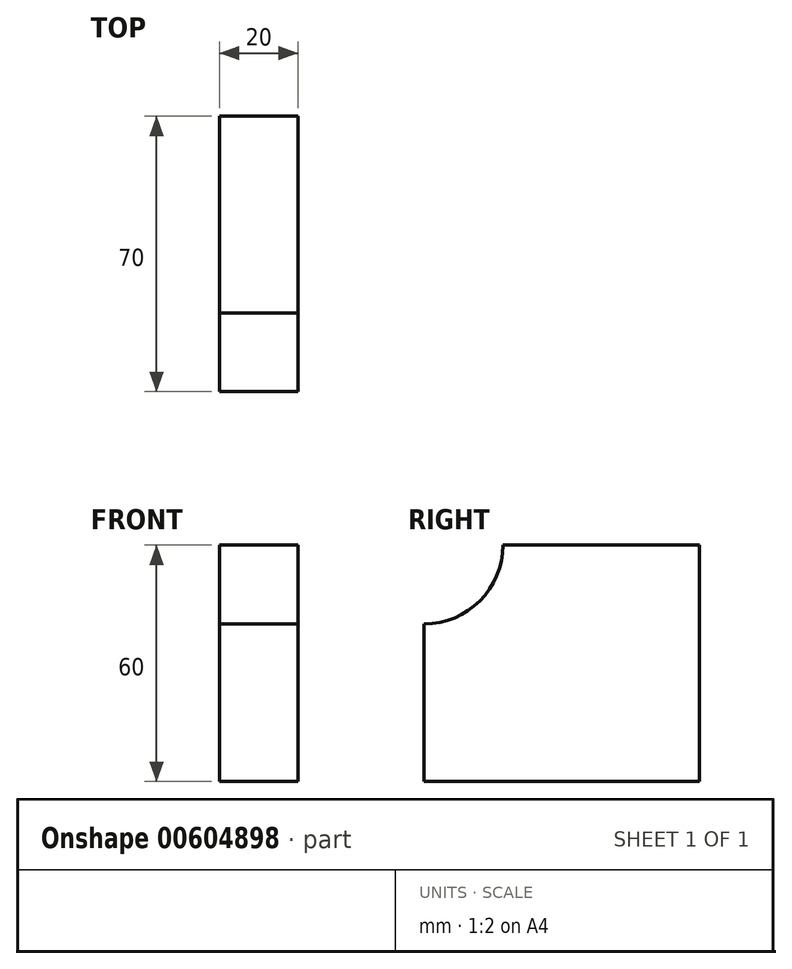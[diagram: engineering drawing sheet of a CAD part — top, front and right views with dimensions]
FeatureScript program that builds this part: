
annotation { "Feature Type Name" : "Feature", "Feature Type Description" : "" }
export const myFeature = defineFeature(function(context is Context, id is Id, definition is map)
    precondition{}
    {
        {
            var Q0;
            Q0=qCreatedBy(makeId("Right.planeOp"),FACE);
            var sketch = newSketch(context, id + "F0", { "sketchPlane" : qUnion([Q0])});
            skLineSegment(sketch, "E0", {"start": v(0, 0) * mm, "end": v(70, 0) * mm});
            skLineSegment(sketch, "E1", {"start": v(70, 0) * mm, "end": v(70, 60) * mm});
            skLineSegment(sketch, "E2", {"start": v(70, 60) * mm, "end": v(20, 60) * mm});
            skLineSegment(sketch, "E3", {"start": v(0, 40) * mm, "end": v(0, 0) * mm});
            skArc(sketch, "E4", {"start": v(0, 40) * mm, "mid": v(14.14, 45.86) * mm, "end": v(20, 60) * mm});
            skSolve(sketch);
        }
        {
            var Q0;
            Q0=makeQuery(id+"F0.imprint","IMPRINT",FACE,{"disambiguationData":[TD([[makeQuery(id+"F0.imprint","IMPRINT",EDGE,{"derivedFrom":sQuery(id+"F0.wireOp",EDGE,"E0")}),1.0]])]});
            extrude(context, id + "F1", {"entities" : qUnion([Q0]), "depth" : 20 * mm, "offsetDistance" : 25 * mm});
        }
    });
